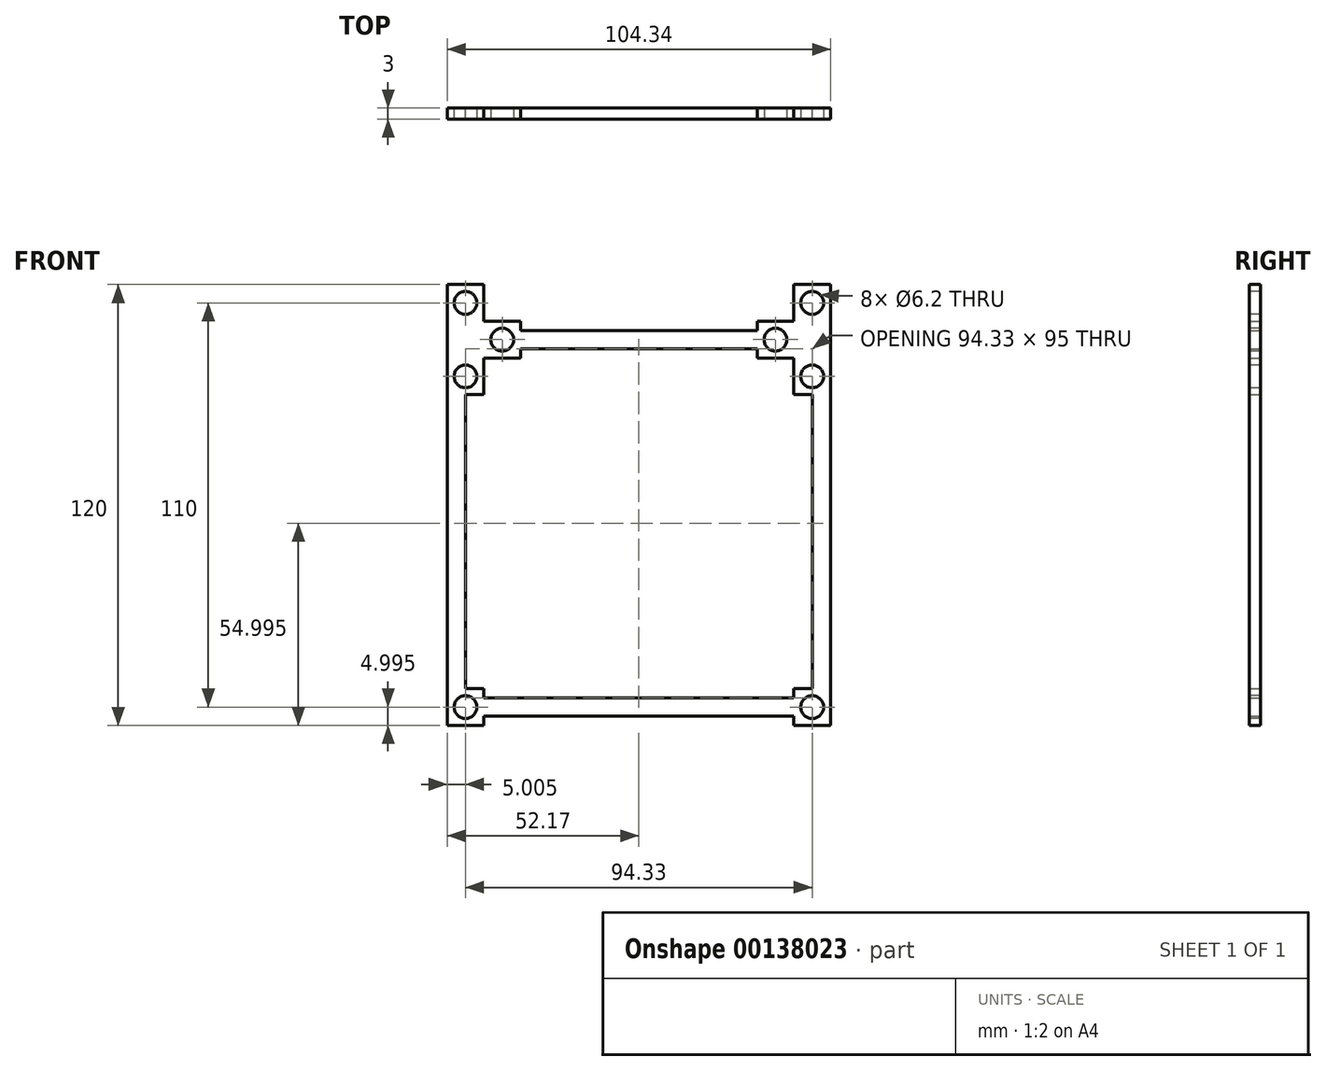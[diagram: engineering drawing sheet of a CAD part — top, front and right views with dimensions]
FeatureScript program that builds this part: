
annotation { "Feature Type Name" : "Feature", "Feature Type Description" : "" }
export const myFeature = defineFeature(function(context is Context, id is Id, definition is map)
    precondition{}
    {
        {
            var Q0;
            Q0=qCreatedBy(makeId("Front.planeOp"),FACE);
            var sketch = newSketch(context, id + "F0", { "sketchPlane" : qUnion([Q0])});
            skLineSegment(sketch, "E0.bottom", {"start": v(-52.17, 55.5) * mm, "end": v(-42.17, 55.5) * mm});
            skLineSegment(sketch, "E0.top", {"start": v(-52.17, 45.5) * mm, "end": v(-42.17, 45.5) * mm});
            skLineSegment(sketch, "E0.left", {"start": v(-52.17, 55.5) * mm, "end": v(-52.17, 45.5) * mm});
            skLineSegment(sketch, "E0.right", {"start": v(-42.16, 55.5) * mm, "end": v(-42.16, 45.5) * mm});
            skLineSegment(sketch, "E1", {"start": v(0, 59.15) * mm, "end": v(0, -57.5) * mm, "construction": true});
            skLineSegment(sketch, "E2", {"start": v(-52.17, 50.5) * mm, "end": v(0, 50.5) * mm, "construction": true});
            skLineSegment(sketch, "E3.bottom", {"start": v(-52.17, 55.5) * mm, "end": v(-42.16, 55.5) * mm});
            skLineSegment(sketch, "E3.top", {"start": v(-52.16, 65.5) * mm, "end": v(-42.16, 65.5) * mm});
            skLineSegment(sketch, "E3.left", {"start": v(-52.16, 55.5) * mm, "end": v(-52.16, 65.5) * mm});
            skLineSegment(sketch, "E3.right", {"start": v(-42.16, 55.5) * mm, "end": v(-42.16, 65.5) * mm});
            skLineSegment(sketch, "E4.bottom", {"start": v(-42.17, 55.5) * mm, "end": v(-32.16, 55.5) * mm});
            skLineSegment(sketch, "E4.top", {"start": v(-42.17, 45.5) * mm, "end": v(-32.16, 45.5) * mm});
            skLineSegment(sketch, "E4.right", {"start": v(-32.16, 55.5) * mm, "end": v(-32.16, 45.5) * mm});
            skLineSegment(sketch, "E5.top", {"start": v(-52.17, 35.5) * mm, "end": v(-42.17, 35.5) * mm});
            skLineSegment(sketch, "E5.left", {"start": v(-52.17, 45.5) * mm, "end": v(-52.17, 35.5) * mm});
            skLineSegment(sketch, "E5.right", {"start": v(-42.17, 45.5) * mm, "end": v(-42.17, 35.5) * mm});
            skPoint(sketch, "E6.oppositeSnap0", {"position": v(-47.17, 35.5) * mm});
            skLineSegment(sketch, "E6.bottom", {"start": v(-52.17, 35.5) * mm, "end": v(-47.17, 35.5) * mm});
            skLineSegment(sketch, "E6.top", {"start": v(-52.17, -44.5) * mm, "end": v(-47.17, -44.5) * mm});
            skLineSegment(sketch, "E6.left", {"start": v(-52.17, 35.5) * mm, "end": v(-52.17, -44.5) * mm});
            skLineSegment(sketch, "E6.right", {"start": v(-47.17, 35.5) * mm, "end": v(-47.17, -44.5) * mm});
            skLineSegment(sketch, "E7.bottom", {"start": v(-52.17, -44.5) * mm, "end": v(-42.16, -44.5) * mm});
            skLineSegment(sketch, "E7.top", {"start": v(-52.17, -54.5) * mm, "end": v(-42.16, -54.5) * mm});
            skLineSegment(sketch, "E7.left", {"start": v(-52.17, -44.5) * mm, "end": v(-52.17, -54.5) * mm});
            skLineSegment(sketch, "E7.right", {"start": v(-42.16, -44.5) * mm, "end": v(-42.16, -54.5) * mm});
            skLineSegment(sketch, "E8.bottom", {"start": v(-42.16, -47) * mm, "end": v(0, -47) * mm});
            skLineSegment(sketch, "E8.top", {"start": v(-42.16, -52) * mm, "end": v(0, -52) * mm});
            skLineSegment(sketch, "E8.left", {"start": v(-42.16, -47) * mm, "end": v(-42.16, -52) * mm});
            skLineSegment(sketch, "E8.right", {"start": v(0, -47) * mm, "end": v(0, -52) * mm});
            skLineSegment(sketch, "E9.bottom", {"start": v(-32.16, 53) * mm, "end": v(0, 53) * mm});
            skLineSegment(sketch, "E9.top", {"start": v(-32.16, 48) * mm, "end": v(0, 48) * mm});
            skLineSegment(sketch, "E9.left", {"start": v(-32.16, 53) * mm, "end": v(-32.16, 48) * mm});
            skLineSegment(sketch, "E9.right", {"start": v(0, 53) * mm, "end": v(0, 48) * mm});
            skPoint(sketch, "E10", {"position": v(-32.16, 50.5) * mm});
            skLineSegment(sketch, "E11", {"start": v(-52.17, -49.5) * mm, "end": v(0, -49.5) * mm, "construction": true});
            skPoint(sketch, "E12", {"position": v(-42.16, -49.5) * mm});
            skLineSegment(sketch, "E13.MirrorCS", {"start": v(42.17, -47) * mm, "end": v(42.17, -52) * mm});
            skLineSegment(sketch, "E14.MirrorCS", {"start": v(32.16, 55.5) * mm, "end": v(32.16, 45.5) * mm});
            skLineSegment(sketch, "E15.MirrorCS", {"start": v(42.17, -44.5) * mm, "end": v(42.17, -54.5) * mm});
            skLineSegment(sketch, "E16.MirrorCS", {"start": v(32.16, 53) * mm, "end": v(32.16, 48) * mm});
            skLineSegment(sketch, "E17.MirrorCS", {"start": v(42.16, 55.5) * mm, "end": v(42.16, 45.5) * mm});
            skLineSegment(sketch, "E18.MirrorCS", {"start": v(52.17, 55.5) * mm, "end": v(42.17, 55.5) * mm});
            skLineSegment(sketch, "E19.MirrorCS", {"start": v(52.17, 45.5) * mm, "end": v(42.17, 45.5) * mm});
            skLineSegment(sketch, "E20.MirrorCS", {"start": v(52.17, -44.5) * mm, "end": v(47.17, -44.5) * mm});
            skLineSegment(sketch, "E21.MirrorCS", {"start": v(52.17, -49.5) * mm, "end": v(0, -49.5) * mm, "construction": true});
            skLineSegment(sketch, "E22.MirrorCS", {"start": v(52.17, 35.5) * mm, "end": v(47.17, 35.5) * mm});
            skLineSegment(sketch, "E23.MirrorCS", {"start": v(32.16, 48) * mm, "end": v(0, 48) * mm});
            skLineSegment(sketch, "E24.MirrorCS", {"start": v(52.17, -44.5) * mm, "end": v(42.17, -44.5) * mm});
            skPoint(sketch, "E25.MirrorP", {"position": v(47.17, 35.5) * mm});
            skPoint(sketch, "E26.MirrorP", {"position": v(42.17, -49.5) * mm});
            skLineSegment(sketch, "E27.MirrorCS", {"start": v(42.17, 45.5) * mm, "end": v(42.17, 35.5) * mm});
            skLineSegment(sketch, "E28.MirrorCS", {"start": v(32.16, 53) * mm, "end": v(0, 53) * mm});
            skLineSegment(sketch, "E29.MirrorCS", {"start": v(47.17, 35.5) * mm, "end": v(47.17, -44.5) * mm});
            skLineSegment(sketch, "E30.MirrorCS", {"start": v(52.17, -44.5) * mm, "end": v(52.17, -54.5) * mm});
            skPoint(sketch, "E31.MirrorP", {"position": v(32.16, 50.5) * mm});
            skLineSegment(sketch, "E32.MirrorCS", {"start": v(52.16, 45.5) * mm, "end": v(52.16, 35.5) * mm});
            skLineSegment(sketch, "E33.MirrorCS", {"start": v(52.16, 35.5) * mm, "end": v(52.17, -44.5) * mm});
            skLineSegment(sketch, "E34.MirrorCS", {"start": v(52.17, -54.5) * mm, "end": v(42.17, -54.5) * mm});
            skLineSegment(sketch, "E35.MirrorCS", {"start": v(42.17, -52) * mm, "end": v(0, -52) * mm});
            skLineSegment(sketch, "E36.MirrorCS", {"start": v(42.17, 45.5) * mm, "end": v(32.16, 45.5) * mm});
            skLineSegment(sketch, "E37.MirrorCS", {"start": v(42.17, 55.5) * mm, "end": v(32.16, 55.5) * mm});
            skLineSegment(sketch, "E38.MirrorCS", {"start": v(42.16, 55.5) * mm, "end": v(42.16, 65.5) * mm});
            skLineSegment(sketch, "E39.MirrorCS", {"start": v(52.16, 55.5) * mm, "end": v(52.16, 65.5) * mm});
            skLineSegment(sketch, "E40.MirrorCS", {"start": v(52.16, 65.5) * mm, "end": v(42.16, 65.5) * mm});
            skLineSegment(sketch, "E41.MirrorCS", {"start": v(52.17, 55.5) * mm, "end": v(42.16, 55.5) * mm});
            skLineSegment(sketch, "E42.MirrorCS", {"start": v(52.17, 50.5) * mm, "end": v(0, 50.5) * mm, "construction": true});
            skLineSegment(sketch, "E43.MirrorCS", {"start": v(52.16, 55.5) * mm, "end": v(52.16, 45.5) * mm});
            skLineSegment(sketch, "E44.MirrorCS", {"start": v(52.17, 35.5) * mm, "end": v(42.17, 35.5) * mm});
            skLineSegment(sketch, "E45.MirrorCS", {"start": v(42.17, -47) * mm, "end": v(0, -47) * mm});
            skLineSegment(sketch, "E46", {"start": v(-47.17, 55.5) * mm, "end": v(-47.17, 45.5) * mm});
            skSolve(sketch);
        }
        {
            var Q0;
            Q0 = qSketchRegion(id + "F0", true);
            extrude(context, id + "F1", {"entities" : qUnion([Q0]), "depth" : 3 * mm});
        }
        {
            var Q0;
            Q0=makeQuery(id+"F1.opExtrude","CAP_FACE",FACE,{"disambiguationData":[OSD([sQuery(id+"F0.wireOp",EDGE,"E0.left"),sQuery(id+"F0.wireOp",EDGE,"E3.top"),sQuery(id+"F0.wireOp",EDGE,"E3.left"),sQuery(id+"F0.wireOp",EDGE,"E3.right"),sQuery(id+"F0.wireOp",EDGE,"E4.bottom"),sQuery(id+"F0.wireOp",EDGE,"E4.top"),sQuery(id+"F0.wireOp",EDGE,"E4.right"),sQuery(id+"F0.wireOp",EDGE,"E5.top"),sQuery(id+"F0.wireOp",EDGE,"E5.left"),sQuery(id+"F0.wireOp",EDGE,"E5.right"),sQuery(id+"F0.wireOp",EDGE,"E6.left"),sQuery(id+"F0.wireOp",EDGE,"E6.right"),sQuery(id+"F0.wireOp",EDGE,"E7.bottom"),sQuery(id+"F0.wireOp",EDGE,"E7.top"),sQuery(id+"F0.wireOp",EDGE,"E7.left"),sQuery(id+"F0.wireOp",EDGE,"E7.right"),sQuery(id+"F0.wireOp",EDGE,"E8.bottom"),sQuery(id+"F0.wireOp",EDGE,"E8.top"),sQuery(id+"F0.wireOp",EDGE,"E9.bottom"),sQuery(id+"F0.wireOp",EDGE,"E9.top"),sQuery(id+"F0.wireOp",EDGE,"E14.MirrorCS"),sQuery(id+"F0.wireOp",EDGE,"E15.MirrorCS"),sQuery(id+"F0.wireOp",EDGE,"E23.MirrorCS"),sQuery(id+"F0.wireOp",EDGE,"E24.MirrorCS"),sQuery(id+"F0.wireOp",EDGE,"E27.MirrorCS"),sQuery(id+"F0.wireOp",EDGE,"E28.MirrorCS"),sQuery(id+"F0.wireOp",EDGE,"E29.MirrorCS"),sQuery(id+"F0.wireOp",EDGE,"E30.MirrorCS"),sQuery(id+"F0.wireOp",EDGE,"E32.MirrorCS"),sQuery(id+"F0.wireOp",EDGE,"E33.MirrorCS"),sQuery(id+"F0.wireOp",EDGE,"E34.MirrorCS"),sQuery(id+"F0.wireOp",EDGE,"E35.MirrorCS"),sQuery(id+"F0.wireOp",EDGE,"E36.MirrorCS"),sQuery(id+"F0.wireOp",EDGE,"E37.MirrorCS"),sQuery(id+"F0.wireOp",EDGE,"E38.MirrorCS"),sQuery(id+"F0.wireOp",EDGE,"E39.MirrorCS"),sQuery(id+"F0.wireOp",EDGE,"E40.MirrorCS"),sQuery(id+"F0.wireOp",EDGE,"E43.MirrorCS"),sQuery(id+"F0.wireOp",EDGE,"E44.MirrorCS"),sQuery(id+"F0.wireOp",EDGE,"E45.MirrorCS")])],"isStart":false});
            var sketch = newSketch(context, id + "F2", { "sketchPlane" : qUnion([Q0])});
            skLineSegment(sketch, "E47", {"start": v(-47.16, 65.5) * mm, "end": v(-47.16, -54.5) * mm, "construction": true});
            skCircle(sketch, "E48", {"center": v(-47.16, 60.5) * mm, "radius": 3.1 * mm});
            skCircle(sketch, "E49", {"center": v(-47.16, 40.5) * mm, "radius": 3.1 * mm});
            skCircle(sketch, "E50", {"center": v(-47.16, -49.5) * mm, "radius": 3.1 * mm});
            skLineSegment(sketch, "E51.0", {"start": v(-52.16, 50.5) * mm, "end": v(0, 50.5) * mm, "construction": true});
            skCircle(sketch, "E52", {"center": v(-37.16, 50.5) * mm, "radius": 3.1 * mm});
            skCircle(sketch, "E53.MirrorC", {"center": v(47.16, 60.5) * mm, "radius": 3.1 * mm});
            skCircle(sketch, "E54.MirrorC", {"center": v(37.16, 50.5) * mm, "radius": 3.1 * mm});
            skCircle(sketch, "E55.MirrorC", {"center": v(47.16, 40.5) * mm, "radius": 3.1 * mm});
            skCircle(sketch, "E56.MirrorC", {"center": v(47.16, -49.5) * mm, "radius": 3.1 * mm});
            skSolve(sketch);
        }
        {
            var Q0;
            Q0 = qSketchRegion(id + "F2", true);
            extrude(context, id + "F3", {"entities" : qUnion([Q0]), "operationType" : NewBodyOperationType.REMOVE, "endBound" : BoundingType.THROUGH_ALL, "oppositeDirection" : true, "depth" : 25 * mm});
        }
    });
